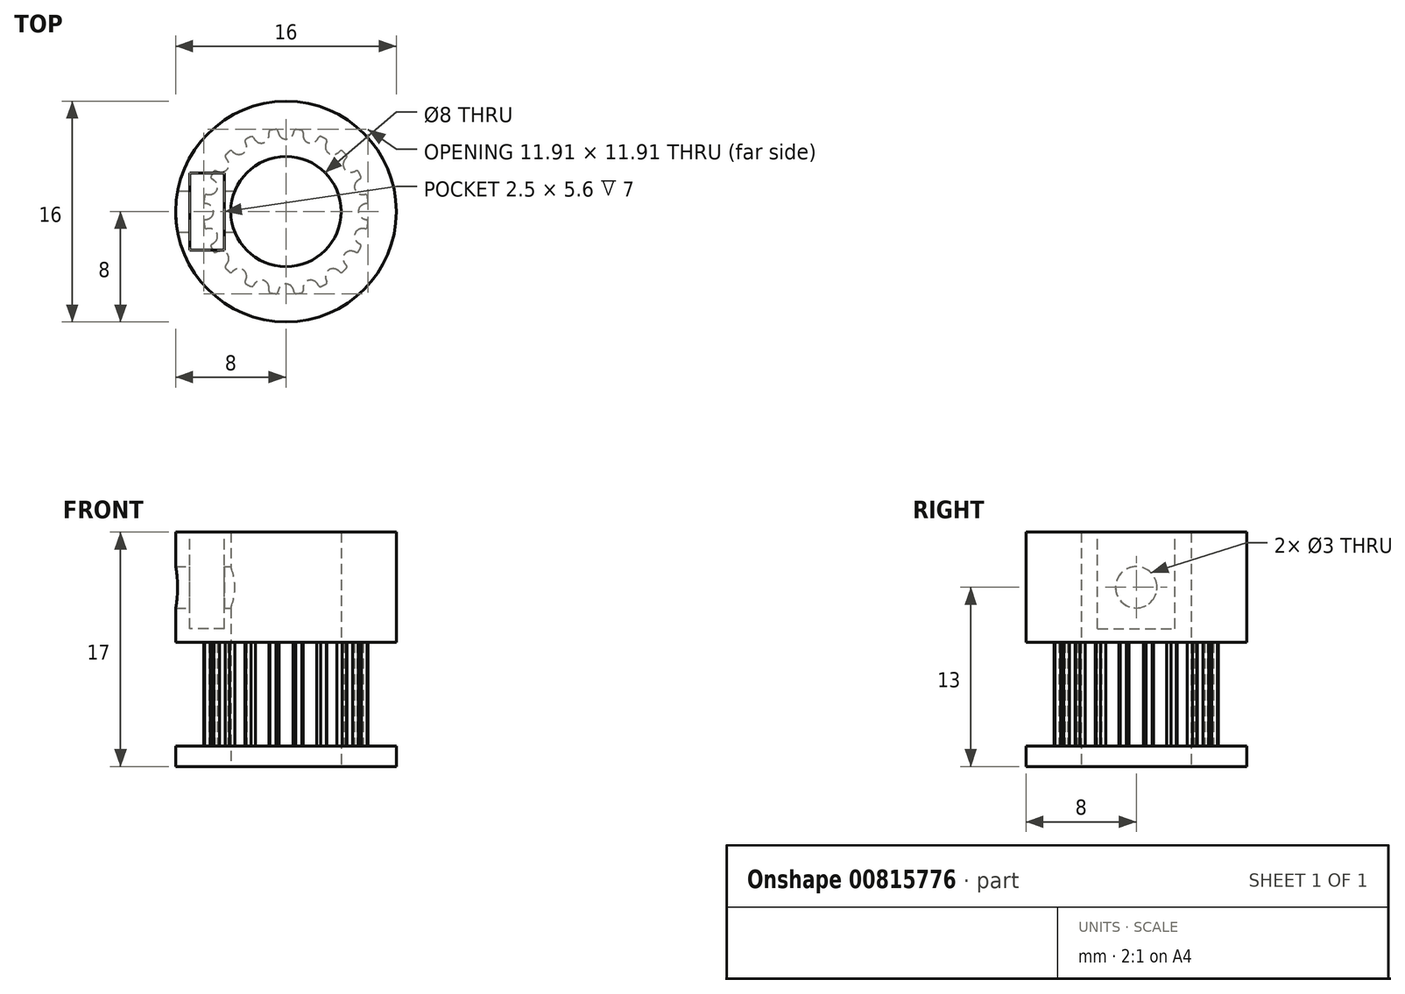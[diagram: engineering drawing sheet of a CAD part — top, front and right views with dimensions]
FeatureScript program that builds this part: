
annotation { "Feature Type Name" : "Feature", "Feature Type Description" : "" }
export const myFeature = defineFeature(function(context is Context, id is Id, definition is map)
    precondition{}
    {
        {
            var Q0;
            Q0=qCreatedBy(makeId("Top.planeOp"),FACE);
            var sketch = newSketch(context, id + "F0", { "sketchPlane" : qUnion([Q0])});
            skLineSegment(sketch, "E0", {"start": v(-19.17, 17.78) * mm, "end": v(-18.17, 17.78) * mm});
            skLineSegment(sketch, "E1", {"start": v(-18.17, 17.78) * mm, "end": v(-18.17, 18.4) * mm});
            skArc(sketch, "E2", {"start": v(-18.67, 18.85) * mm, "mid": v(-18.88, 19.07) * mm, "end": v(-19.17, 19.16) * mm});
            skArc(sketch, "E3", {"start": v(-18.58, 18.54) * mm, "mid": v(-18.61, 18.7) * mm, "end": v(-18.67, 18.85) * mm});
            skArc(sketch, "E4", {"start": v(-18.58, 18.54) * mm, "mid": v(-18.53, 18.44) * mm, "end": v(-18.43, 18.4) * mm});
            skLineSegment(sketch, "E5", {"start": v(-18.43, 18.4) * mm, "end": v(-18.17, 18.4) * mm});
            skArc(sketch, "E6.0.MirrorCS", {"start": v(-19.67, 18.85) * mm, "mid": v(-19.47, 19.07) * mm, "end": v(-19.17, 19.16) * mm});
            skArc(sketch, "E7.0.MirrorCS", {"start": v(-19.76, 18.54) * mm, "mid": v(-19.73, 18.7) * mm, "end": v(-19.67, 18.85) * mm});
            skArc(sketch, "E8.0.MirrorCS", {"start": v(-19.76, 18.54) * mm, "mid": v(-19.81, 18.44) * mm, "end": v(-19.91, 18.4) * mm});
            skLineSegment(sketch, "E9.0.MirrorCS", {"start": v(-19.91, 18.4) * mm, "end": v(-20.17, 18.4) * mm});
            skLineSegment(sketch, "E10.0.MirrorCS", {"start": v(-20.17, 17.78) * mm, "end": v(-20.17, 18.4) * mm});
            skLineSegment(sketch, "E11.0.MirrorCS", {"start": v(-19.17, 17.78) * mm, "end": v(-20.17, 17.78) * mm});
            skLineSegment(sketch, "E12.direction1", {"start": v(-20.17, 17.78) * mm, "end": v(-18.17, 17.78) * mm, "construction": true});
            skLineSegment(sketch, "E13", {"start": v(-20.17, 18.15) * mm, "end": v(-18.17, 18.15) * mm, "construction": true});
            skPoint(sketch, "E14", {"position": v(0, -5.25) * mm});
            skArc(sketch, "E15", {"start": v(0.51, -5.6) * mm, "mid": v(0, -5.25) * mm, "end": v(-0.51, -5.6) * mm});
            skArc(sketch, "E16", {"start": v(-0.51, -5.6) * mm, "mid": v(-0.56, -5.71) * mm, "end": v(-0.59, -5.83) * mm});
            skArc(sketch, "E17", {"start": v(0.59, -5.83) * mm, "mid": v(0.56, -5.71) * mm, "end": v(0.51, -5.6) * mm});
            skArc(sketch, "E18", {"start": v(0.72, -5.96) * mm, "mid": v(0.94, -5.93) * mm, "end": v(1.16, -5.89) * mm});
            skArc(sketch, "E19", {"start": v(0.59, -5.83) * mm, "mid": v(0.66, -5.94) * mm, "end": v(0.8, -5.95) * mm});
            skArc(sketch, "E20", {"start": v(-0.59, -5.83) * mm, "mid": v(-0.66, -5.94) * mm, "end": v(-0.8, -5.95) * mm});
            skArc(sketch, "E21.1.0", {"start": v(2.22, -5.16) * mm, "mid": v(1.62, -5) * mm, "end": v(1.24, -5.48) * mm});
            skPoint(sketch, "E21.1.1", {"position": v(1.62, -5) * mm});
            skArc(sketch, "E21.1.2", {"start": v(1.24, -5.48) * mm, "mid": v(1.23, -5.6) * mm, "end": v(1.24, -5.73) * mm});
            skArc(sketch, "E21.1.3", {"start": v(2.36, -5.37) * mm, "mid": v(2.47, -5.44) * mm, "end": v(2.6, -5.41) * mm});
            skArc(sketch, "E21.1.4", {"start": v(1.24, -5.73) * mm, "mid": v(1.2, -5.85) * mm, "end": v(1.08, -5.9) * mm});
            skArc(sketch, "E21.1.5", {"start": v(2.36, -5.37) * mm, "mid": v(2.3, -5.26) * mm, "end": v(2.22, -5.16) * mm});
            skArc(sketch, "E22.3.2.0", {"start": v(3.7, -4.22) * mm, "mid": v(3.09, -4.25) * mm, "end": v(2.87, -4.83) * mm});
            skPoint(sketch, "E22.4.2.0", {"position": v(3.09, -4.25) * mm});
            skArc(sketch, "E22.5.2.0", {"start": v(2.87, -4.83) * mm, "mid": v(2.9, -4.95) * mm, "end": v(2.95, -5.07) * mm});
            skArc(sketch, "E22.9.2.0", {"start": v(3.9, -4.37) * mm, "mid": v(4.03, -4.41) * mm, "end": v(4.14, -4.35) * mm});
            skArc(sketch, "E22.13.2.0", {"start": v(2.95, -5.07) * mm, "mid": v(2.95, -5.2) * mm, "end": v(2.85, -5.28) * mm});
            skArc(sketch, "E22.17.2.0", {"start": v(3.9, -4.37) * mm, "mid": v(3.81, -4.3) * mm, "end": v(3.7, -4.22) * mm});
            skArc(sketch, "E22.3.3.0", {"start": v(4.83, -2.87) * mm, "mid": v(4.25, -3.09) * mm, "end": v(4.22, -3.7) * mm});
            skPoint(sketch, "E22.4.3.0", {"position": v(4.25, -3.09) * mm});
            skArc(sketch, "E22.5.3.0", {"start": v(4.22, -3.7) * mm, "mid": v(4.3, -3.81) * mm, "end": v(4.37, -3.9) * mm});
            skArc(sketch, "E22.9.3.0", {"start": v(5.07, -2.95) * mm, "mid": v(5.2, -2.95) * mm, "end": v(5.28, -2.85) * mm});
            skArc(sketch, "E22.13.3.0", {"start": v(4.37, -3.9) * mm, "mid": v(4.41, -4.03) * mm, "end": v(4.35, -4.14) * mm});
            skArc(sketch, "E22.17.3.0", {"start": v(5.07, -2.95) * mm, "mid": v(4.95, -2.9) * mm, "end": v(4.83, -2.87) * mm});
            skArc(sketch, "E22.3.4.0", {"start": v(5.48, -1.24) * mm, "mid": v(5, -1.62) * mm, "end": v(5.16, -2.22) * mm});
            skPoint(sketch, "E22.4.4.0", {"position": v(5, -1.62) * mm});
            skArc(sketch, "E22.5.4.0", {"start": v(5.16, -2.22) * mm, "mid": v(5.26, -2.3) * mm, "end": v(5.37, -2.36) * mm});
            skArc(sketch, "E22.9.4.0", {"start": v(5.73, -1.24) * mm, "mid": v(5.85, -1.2) * mm, "end": v(5.9, -1.08) * mm});
            skArc(sketch, "E22.13.4.0", {"start": v(5.37, -2.36) * mm, "mid": v(5.44, -2.47) * mm, "end": v(5.41, -2.6) * mm});
            skArc(sketch, "E22.17.4.0", {"start": v(5.73, -1.24) * mm, "mid": v(5.6, -1.23) * mm, "end": v(5.48, -1.24) * mm});
            skArc(sketch, "E22.3.5.0", {"start": v(5.6, 0.51) * mm, "mid": v(5.25, 0) * mm, "end": v(5.6, -0.51) * mm});
            skPoint(sketch, "E22.4.5.0", {"position": v(5.25, 0) * mm});
            skArc(sketch, "E22.5.5.0", {"start": v(5.6, -0.51) * mm, "mid": v(5.71, -0.56) * mm, "end": v(5.83, -0.59) * mm});
            skArc(sketch, "E22.9.5.0", {"start": v(5.83, 0.59) * mm, "mid": v(5.94, 0.66) * mm, "end": v(5.95, 0.8) * mm});
            skArc(sketch, "E22.13.5.0", {"start": v(5.83, -0.59) * mm, "mid": v(5.94, -0.66) * mm, "end": v(5.95, -0.8) * mm});
            skArc(sketch, "E22.17.5.0", {"start": v(5.83, 0.59) * mm, "mid": v(5.71, 0.56) * mm, "end": v(5.6, 0.51) * mm});
            skArc(sketch, "E22.3.6.0", {"start": v(5.16, 2.22) * mm, "mid": v(5, 1.62) * mm, "end": v(5.48, 1.24) * mm});
            skPoint(sketch, "E22.4.6.0", {"position": v(5, 1.62) * mm});
            skArc(sketch, "E22.5.6.0", {"start": v(5.48, 1.24) * mm, "mid": v(5.6, 1.23) * mm, "end": v(5.73, 1.24) * mm});
            skArc(sketch, "E22.9.6.0", {"start": v(5.37, 2.36) * mm, "mid": v(5.44, 2.47) * mm, "end": v(5.41, 2.6) * mm});
            skArc(sketch, "E22.13.6.0", {"start": v(5.73, 1.24) * mm, "mid": v(5.85, 1.2) * mm, "end": v(5.9, 1.08) * mm});
            skArc(sketch, "E22.17.6.0", {"start": v(5.37, 2.36) * mm, "mid": v(5.26, 2.3) * mm, "end": v(5.16, 2.22) * mm});
            skArc(sketch, "E22.3.7.0", {"start": v(4.22, 3.7) * mm, "mid": v(4.25, 3.09) * mm, "end": v(4.83, 2.87) * mm});
            skPoint(sketch, "E22.4.7.0", {"position": v(4.25, 3.09) * mm});
            skArc(sketch, "E22.5.7.0", {"start": v(4.83, 2.87) * mm, "mid": v(4.95, 2.9) * mm, "end": v(5.07, 2.95) * mm});
            skArc(sketch, "E22.9.7.0", {"start": v(4.37, 3.9) * mm, "mid": v(4.41, 4.03) * mm, "end": v(4.35, 4.14) * mm});
            skArc(sketch, "E22.13.7.0", {"start": v(5.07, 2.95) * mm, "mid": v(5.2, 2.95) * mm, "end": v(5.28, 2.85) * mm});
            skArc(sketch, "E22.17.7.0", {"start": v(4.37, 3.9) * mm, "mid": v(4.3, 3.81) * mm, "end": v(4.22, 3.7) * mm});
            skArc(sketch, "E22.3.8.0", {"start": v(2.87, 4.83) * mm, "mid": v(3.09, 4.25) * mm, "end": v(3.7, 4.22) * mm});
            skPoint(sketch, "E22.4.8.0", {"position": v(3.09, 4.25) * mm});
            skArc(sketch, "E22.5.8.0", {"start": v(3.7, 4.22) * mm, "mid": v(3.81, 4.3) * mm, "end": v(3.9, 4.37) * mm});
            skArc(sketch, "E22.9.8.0", {"start": v(2.95, 5.07) * mm, "mid": v(2.95, 5.2) * mm, "end": v(2.85, 5.28) * mm});
            skArc(sketch, "E22.13.8.0", {"start": v(3.9, 4.37) * mm, "mid": v(4.03, 4.41) * mm, "end": v(4.14, 4.35) * mm});
            skArc(sketch, "E22.17.8.0", {"start": v(2.95, 5.07) * mm, "mid": v(2.9, 4.95) * mm, "end": v(2.87, 4.83) * mm});
            skArc(sketch, "E22.3.9.0", {"start": v(1.24, 5.48) * mm, "mid": v(1.62, 5) * mm, "end": v(2.22, 5.16) * mm});
            skPoint(sketch, "E22.4.9.0", {"position": v(1.62, 5) * mm});
            skArc(sketch, "E22.5.9.0", {"start": v(2.22, 5.16) * mm, "mid": v(2.3, 5.26) * mm, "end": v(2.36, 5.37) * mm});
            skArc(sketch, "E22.9.9.0", {"start": v(1.24, 5.73) * mm, "mid": v(1.2, 5.85) * mm, "end": v(1.08, 5.9) * mm});
            skArc(sketch, "E22.13.9.0", {"start": v(2.36, 5.37) * mm, "mid": v(2.47, 5.44) * mm, "end": v(2.6, 5.41) * mm});
            skArc(sketch, "E22.17.9.0", {"start": v(1.24, 5.73) * mm, "mid": v(1.23, 5.6) * mm, "end": v(1.24, 5.48) * mm});
            skArc(sketch, "E22.3.10.0", {"start": v(-0.51, 5.6) * mm, "mid": v(0, 5.25) * mm, "end": v(0.51, 5.6) * mm});
            skPoint(sketch, "E22.4.10.0", {"position": v(0, 5.25) * mm});
            skArc(sketch, "E22.5.10.0", {"start": v(0.51, 5.6) * mm, "mid": v(0.56, 5.71) * mm, "end": v(0.59, 5.83) * mm});
            skArc(sketch, "E22.9.10.0", {"start": v(-0.59, 5.83) * mm, "mid": v(-0.66, 5.94) * mm, "end": v(-0.8, 5.95) * mm});
            skArc(sketch, "E22.13.10.0", {"start": v(0.59, 5.83) * mm, "mid": v(0.66, 5.94) * mm, "end": v(0.8, 5.95) * mm});
            skArc(sketch, "E22.17.10.0", {"start": v(-0.59, 5.83) * mm, "mid": v(-0.56, 5.71) * mm, "end": v(-0.51, 5.6) * mm});
            skArc(sketch, "E22.3.11.0", {"start": v(-2.22, 5.16) * mm, "mid": v(-1.62, 5) * mm, "end": v(-1.24, 5.48) * mm});
            skPoint(sketch, "E22.4.11.0", {"position": v(-1.62, 5) * mm});
            skArc(sketch, "E22.5.11.0", {"start": v(-1.24, 5.48) * mm, "mid": v(-1.23, 5.6) * mm, "end": v(-1.24, 5.73) * mm});
            skArc(sketch, "E22.9.11.0", {"start": v(-2.36, 5.37) * mm, "mid": v(-2.47, 5.44) * mm, "end": v(-2.6, 5.41) * mm});
            skArc(sketch, "E22.13.11.0", {"start": v(-1.24, 5.73) * mm, "mid": v(-1.2, 5.85) * mm, "end": v(-1.08, 5.9) * mm});
            skArc(sketch, "E22.17.11.0", {"start": v(-2.36, 5.37) * mm, "mid": v(-2.3, 5.26) * mm, "end": v(-2.22, 5.16) * mm});
            skArc(sketch, "E22.3.12.0", {"start": v(-3.7, 4.22) * mm, "mid": v(-3.09, 4.25) * mm, "end": v(-2.87, 4.83) * mm});
            skPoint(sketch, "E22.4.12.0", {"position": v(-3.09, 4.25) * mm});
            skArc(sketch, "E22.5.12.0", {"start": v(-2.87, 4.83) * mm, "mid": v(-2.9, 4.95) * mm, "end": v(-2.95, 5.07) * mm});
            skArc(sketch, "E22.9.12.0", {"start": v(-3.9, 4.37) * mm, "mid": v(-4.03, 4.41) * mm, "end": v(-4.14, 4.35) * mm});
            skArc(sketch, "E22.13.12.0", {"start": v(-2.95, 5.07) * mm, "mid": v(-2.95, 5.2) * mm, "end": v(-2.85, 5.28) * mm});
            skArc(sketch, "E22.17.12.0", {"start": v(-3.9, 4.37) * mm, "mid": v(-3.81, 4.3) * mm, "end": v(-3.7, 4.22) * mm});
            skArc(sketch, "E22.3.13.0", {"start": v(-4.83, 2.87) * mm, "mid": v(-4.25, 3.09) * mm, "end": v(-4.22, 3.7) * mm});
            skPoint(sketch, "E22.4.13.0", {"position": v(-4.25, 3.09) * mm});
            skArc(sketch, "E22.5.13.0", {"start": v(-4.22, 3.7) * mm, "mid": v(-4.3, 3.81) * mm, "end": v(-4.37, 3.9) * mm});
            skArc(sketch, "E22.9.13.0", {"start": v(-5.07, 2.95) * mm, "mid": v(-5.2, 2.95) * mm, "end": v(-5.28, 2.85) * mm});
            skArc(sketch, "E22.13.13.0", {"start": v(-4.37, 3.9) * mm, "mid": v(-4.41, 4.03) * mm, "end": v(-4.35, 4.14) * mm});
            skArc(sketch, "E22.17.13.0", {"start": v(-5.07, 2.95) * mm, "mid": v(-4.95, 2.9) * mm, "end": v(-4.83, 2.87) * mm});
            skArc(sketch, "E22.3.14.0", {"start": v(-5.48, 1.24) * mm, "mid": v(-5, 1.62) * mm, "end": v(-5.16, 2.22) * mm});
            skPoint(sketch, "E22.4.14.0", {"position": v(-5, 1.62) * mm});
            skArc(sketch, "E22.5.14.0", {"start": v(-5.16, 2.22) * mm, "mid": v(-5.26, 2.3) * mm, "end": v(-5.37, 2.36) * mm});
            skArc(sketch, "E22.9.14.0", {"start": v(-5.73, 1.24) * mm, "mid": v(-5.85, 1.2) * mm, "end": v(-5.9, 1.08) * mm});
            skArc(sketch, "E22.13.14.0", {"start": v(-5.37, 2.36) * mm, "mid": v(-5.44, 2.47) * mm, "end": v(-5.41, 2.6) * mm});
            skArc(sketch, "E22.17.14.0", {"start": v(-5.73, 1.24) * mm, "mid": v(-5.6, 1.23) * mm, "end": v(-5.48, 1.24) * mm});
            skArc(sketch, "E22.3.15.0", {"start": v(-5.6, -0.51) * mm, "mid": v(-5.25, 0) * mm, "end": v(-5.6, 0.51) * mm});
            skPoint(sketch, "E22.4.15.0", {"position": v(-5.25, 0) * mm});
            skArc(sketch, "E22.5.15.0", {"start": v(-5.6, 0.51) * mm, "mid": v(-5.71, 0.56) * mm, "end": v(-5.83, 0.59) * mm});
            skArc(sketch, "E22.9.15.0", {"start": v(-5.83, -0.59) * mm, "mid": v(-5.94, -0.66) * mm, "end": v(-5.95, -0.8) * mm});
            skArc(sketch, "E22.13.15.0", {"start": v(-5.83, 0.59) * mm, "mid": v(-5.94, 0.66) * mm, "end": v(-5.95, 0.8) * mm});
            skArc(sketch, "E22.17.15.0", {"start": v(-5.83, -0.59) * mm, "mid": v(-5.71, -0.56) * mm, "end": v(-5.6, -0.51) * mm});
            skArc(sketch, "E22.3.16.0", {"start": v(-5.16, -2.22) * mm, "mid": v(-5, -1.62) * mm, "end": v(-5.48, -1.24) * mm});
            skPoint(sketch, "E22.4.16.0", {"position": v(-5, -1.62) * mm});
            skArc(sketch, "E22.5.16.0", {"start": v(-5.48, -1.24) * mm, "mid": v(-5.6, -1.23) * mm, "end": v(-5.73, -1.24) * mm});
            skArc(sketch, "E22.9.16.0", {"start": v(-5.37, -2.36) * mm, "mid": v(-5.44, -2.47) * mm, "end": v(-5.41, -2.6) * mm});
            skArc(sketch, "E22.13.16.0", {"start": v(-5.73, -1.24) * mm, "mid": v(-5.85, -1.2) * mm, "end": v(-5.9, -1.08) * mm});
            skArc(sketch, "E22.17.16.0", {"start": v(-5.37, -2.36) * mm, "mid": v(-5.26, -2.3) * mm, "end": v(-5.16, -2.22) * mm});
            skArc(sketch, "E22.3.17.0", {"start": v(-4.22, -3.7) * mm, "mid": v(-4.25, -3.09) * mm, "end": v(-4.83, -2.87) * mm});
            skPoint(sketch, "E22.4.17.0", {"position": v(-4.25, -3.09) * mm});
            skArc(sketch, "E22.5.17.0", {"start": v(-4.83, -2.87) * mm, "mid": v(-4.95, -2.9) * mm, "end": v(-5.07, -2.95) * mm});
            skArc(sketch, "E22.9.17.0", {"start": v(-4.37, -3.9) * mm, "mid": v(-4.41, -4.03) * mm, "end": v(-4.35, -4.14) * mm});
            skArc(sketch, "E22.13.17.0", {"start": v(-5.07, -2.95) * mm, "mid": v(-5.2, -2.95) * mm, "end": v(-5.28, -2.85) * mm});
            skArc(sketch, "E22.17.17.0", {"start": v(-4.37, -3.9) * mm, "mid": v(-4.3, -3.81) * mm, "end": v(-4.22, -3.7) * mm});
            skArc(sketch, "E22.3.18.0", {"start": v(-2.87, -4.83) * mm, "mid": v(-3.09, -4.25) * mm, "end": v(-3.7, -4.22) * mm});
            skPoint(sketch, "E22.4.18.0", {"position": v(-3.09, -4.25) * mm});
            skArc(sketch, "E22.5.18.0", {"start": v(-3.7, -4.22) * mm, "mid": v(-3.81, -4.3) * mm, "end": v(-3.9, -4.37) * mm});
            skArc(sketch, "E22.9.18.0", {"start": v(-2.95, -5.07) * mm, "mid": v(-2.95, -5.2) * mm, "end": v(-2.85, -5.28) * mm});
            skArc(sketch, "E22.13.18.0", {"start": v(-3.9, -4.37) * mm, "mid": v(-4.03, -4.41) * mm, "end": v(-4.14, -4.35) * mm});
            skArc(sketch, "E22.17.18.0", {"start": v(-2.95, -5.07) * mm, "mid": v(-2.9, -4.95) * mm, "end": v(-2.87, -4.83) * mm});
            skArc(sketch, "E22.3.19.0", {"start": v(-1.24, -5.48) * mm, "mid": v(-1.62, -5) * mm, "end": v(-2.22, -5.16) * mm});
            skPoint(sketch, "E22.4.19.0", {"position": v(-1.62, -5) * mm});
            skArc(sketch, "E22.5.19.0", {"start": v(-2.22, -5.16) * mm, "mid": v(-2.3, -5.26) * mm, "end": v(-2.36, -5.37) * mm});
            skArc(sketch, "E22.9.19.0", {"start": v(-1.24, -5.73) * mm, "mid": v(-1.2, -5.85) * mm, "end": v(-1.08, -5.9) * mm});
            skArc(sketch, "E22.13.19.0", {"start": v(-2.36, -5.37) * mm, "mid": v(-2.47, -5.44) * mm, "end": v(-2.6, -5.41) * mm});
            skArc(sketch, "E22.17.19.0", {"start": v(-1.24, -5.73) * mm, "mid": v(-1.23, -5.6) * mm, "end": v(-1.24, -5.48) * mm});
            skArc(sketch, "E23.trimOffspring", {"start": v(2.52, -5.44) * mm, "mid": v(2.72, -5.35) * mm, "end": v(2.92, -5.24) * mm});
            skArc(sketch, "E24.trimOffspring", {"start": v(4.08, -4.4) * mm, "mid": v(4.24, -4.24) * mm, "end": v(4.4, -4.08) * mm});
            skArc(sketch, "E25.trimOffspring", {"start": v(5.24, -2.92) * mm, "mid": v(5.33, -2.76) * mm, "end": v(5.41, -2.6) * mm});
            skArc(sketch, "E26.trimOffspring", {"start": v(5.89, -1.16) * mm, "mid": v(5.93, -0.94) * mm, "end": v(5.96, -0.72) * mm});
            skArc(sketch, "E27.trimOffspring", {"start": v(5.44, 2.52) * mm, "mid": v(5.35, 2.72) * mm, "end": v(5.24, 2.92) * mm});
            skArc(sketch, "E28.trimOffspring", {"start": v(4.4, 4.08) * mm, "mid": v(4.24, 4.24) * mm, "end": v(4.08, 4.4) * mm});
            skArc(sketch, "E29.trimOffspring", {"start": v(5.96, 0.72) * mm, "mid": v(5.93, 0.94) * mm, "end": v(5.89, 1.16) * mm});
            skArc(sketch, "E30.trimOffspring", {"start": v(2.92, 5.24) * mm, "mid": v(2.72, 5.35) * mm, "end": v(2.52, 5.44) * mm});
            skArc(sketch, "E31.trimOffspring", {"start": v(1.16, 5.89) * mm, "mid": v(0.94, 5.93) * mm, "end": v(0.72, 5.96) * mm});
            skArc(sketch, "E32.trimOffspring", {"start": v(-0.72, 5.96) * mm, "mid": v(-0.94, 5.93) * mm, "end": v(-1.16, 5.89) * mm});
            skArc(sketch, "E33.trimOffspring", {"start": v(-2.52, 5.44) * mm, "mid": v(-2.72, 5.35) * mm, "end": v(-2.92, 5.24) * mm});
            skArc(sketch, "E34.trimOffspring", {"start": v(-4.08, 4.4) * mm, "mid": v(-4.24, 4.24) * mm, "end": v(-4.4, 4.08) * mm});
            skArc(sketch, "E35.trimOffspring", {"start": v(-5.24, 2.92) * mm, "mid": v(-5.35, 2.72) * mm, "end": v(-5.44, 2.52) * mm});
            skArc(sketch, "E36.trimOffspring", {"start": v(-5.89, 1.16) * mm, "mid": v(-5.93, 0.94) * mm, "end": v(-5.96, 0.72) * mm});
            skArc(sketch, "E37.trimOffspring", {"start": v(-5.96, -0.72) * mm, "mid": v(-5.93, -0.94) * mm, "end": v(-5.89, -1.16) * mm});
            skArc(sketch, "E38.trimOffspring", {"start": v(-5.44, -2.52) * mm, "mid": v(-5.35, -2.72) * mm, "end": v(-5.24, -2.92) * mm});
            skArc(sketch, "E39.trimOffspring", {"start": v(-4.4, -4.08) * mm, "mid": v(-4.24, -4.24) * mm, "end": v(-4.08, -4.4) * mm});
            skArc(sketch, "E40.trimOffspring", {"start": v(-2.92, -5.24) * mm, "mid": v(-2.72, -5.35) * mm, "end": v(-2.52, -5.44) * mm});
            skArc(sketch, "E41.trimOffspring", {"start": v(-1.16, -5.89) * mm, "mid": v(-0.94, -5.93) * mm, "end": v(-0.72, -5.96) * mm});
            skSolve(sketch);
        }
        {
            var Q0;
            Q0=makeQuery(id+"F0.imprint","IMPRINT",FACE,{"disambiguationData":[TD([[makeQuery(id+"F0.imprint","IMPRINT",EDGE,{"derivedFrom":sQuery(id+"F0.wireOp",EDGE,"E15")}),-1.0]])]});
            extrude(context, id + "F1", {"entities" : qUnion([Q0]), "depth" : 7.5 * mm});
        }
        {
            var Q0;
            Q0=makeQuery(id+"F1.opExtrude","CAP_FACE",FACE,{"disambiguationData":[OSD([sQuery(id+"F0.wireOp",EDGE,"E15"),sQuery(id+"F0.wireOp",EDGE,"E16"),sQuery(id+"F0.wireOp",EDGE,"E17"),sQuery(id+"F0.wireOp",EDGE,"E18"),sQuery(id+"F0.wireOp",EDGE,"E19"),sQuery(id+"F0.wireOp",EDGE,"E20"),sQuery(id+"F0.wireOp",EDGE,"E21.1.0"),sQuery(id+"F0.wireOp",EDGE,"E21.1.2"),sQuery(id+"F0.wireOp",EDGE,"E21.1.3"),sQuery(id+"F0.wireOp",EDGE,"E21.1.4"),sQuery(id+"F0.wireOp",EDGE,"E21.1.5"),sQuery(id+"F0.wireOp",EDGE,"E22.3.2.0"),sQuery(id+"F0.wireOp",EDGE,"E22.5.2.0"),sQuery(id+"F0.wireOp",EDGE,"E22.9.2.0"),sQuery(id+"F0.wireOp",EDGE,"E22.13.2.0"),sQuery(id+"F0.wireOp",EDGE,"E22.17.2.0"),sQuery(id+"F0.wireOp",EDGE,"E22.3.3.0"),sQuery(id+"F0.wireOp",EDGE,"E22.5.3.0"),sQuery(id+"F0.wireOp",EDGE,"E22.9.3.0"),sQuery(id+"F0.wireOp",EDGE,"E22.13.3.0"),sQuery(id+"F0.wireOp",EDGE,"E22.17.3.0"),sQuery(id+"F0.wireOp",EDGE,"E22.3.4.0"),sQuery(id+"F0.wireOp",EDGE,"E22.5.4.0"),sQuery(id+"F0.wireOp",EDGE,"E22.9.4.0"),sQuery(id+"F0.wireOp",EDGE,"E22.13.4.0"),sQuery(id+"F0.wireOp",EDGE,"E22.17.4.0"),sQuery(id+"F0.wireOp",EDGE,"E22.3.5.0"),sQuery(id+"F0.wireOp",EDGE,"E22.5.5.0"),sQuery(id+"F0.wireOp",EDGE,"E22.9.5.0"),sQuery(id+"F0.wireOp",EDGE,"E22.13.5.0"),sQuery(id+"F0.wireOp",EDGE,"E22.17.5.0"),sQuery(id+"F0.wireOp",EDGE,"E22.3.6.0"),sQuery(id+"F0.wireOp",EDGE,"E22.5.6.0"),sQuery(id+"F0.wireOp",EDGE,"E22.9.6.0"),sQuery(id+"F0.wireOp",EDGE,"E22.13.6.0"),sQuery(id+"F0.wireOp",EDGE,"E22.17.6.0"),sQuery(id+"F0.wireOp",EDGE,"E22.3.7.0"),sQuery(id+"F0.wireOp",EDGE,"E22.5.7.0"),sQuery(id+"F0.wireOp",EDGE,"E22.9.7.0"),sQuery(id+"F0.wireOp",EDGE,"E22.13.7.0"),sQuery(id+"F0.wireOp",EDGE,"E22.17.7.0"),sQuery(id+"F0.wireOp",EDGE,"E22.3.8.0"),sQuery(id+"F0.wireOp",EDGE,"E22.5.8.0"),sQuery(id+"F0.wireOp",EDGE,"E22.9.8.0"),sQuery(id+"F0.wireOp",EDGE,"E22.13.8.0"),sQuery(id+"F0.wireOp",EDGE,"E22.17.8.0"),sQuery(id+"F0.wireOp",EDGE,"E22.3.9.0"),sQuery(id+"F0.wireOp",EDGE,"E22.5.9.0"),sQuery(id+"F0.wireOp",EDGE,"E22.9.9.0"),sQuery(id+"F0.wireOp",EDGE,"E22.13.9.0"),sQuery(id+"F0.wireOp",EDGE,"E22.17.9.0"),sQuery(id+"F0.wireOp",EDGE,"E22.3.10.0"),sQuery(id+"F0.wireOp",EDGE,"E22.5.10.0"),sQuery(id+"F0.wireOp",EDGE,"E22.9.10.0"),sQuery(id+"F0.wireOp",EDGE,"E22.13.10.0"),sQuery(id+"F0.wireOp",EDGE,"E22.17.10.0"),sQuery(id+"F0.wireOp",EDGE,"E22.3.11.0"),sQuery(id+"F0.wireOp",EDGE,"E22.5.11.0"),sQuery(id+"F0.wireOp",EDGE,"E22.9.11.0"),sQuery(id+"F0.wireOp",EDGE,"E22.13.11.0"),sQuery(id+"F0.wireOp",EDGE,"E22.17.11.0"),sQuery(id+"F0.wireOp",EDGE,"E22.3.12.0"),sQuery(id+"F0.wireOp",EDGE,"E22.5.12.0"),sQuery(id+"F0.wireOp",EDGE,"E22.9.12.0"),sQuery(id+"F0.wireOp",EDGE,"E22.13.12.0"),sQuery(id+"F0.wireOp",EDGE,"E22.17.12.0"),sQuery(id+"F0.wireOp",EDGE,"E22.3.13.0"),sQuery(id+"F0.wireOp",EDGE,"E22.5.13.0"),sQuery(id+"F0.wireOp",EDGE,"E22.9.13.0"),sQuery(id+"F0.wireOp",EDGE,"E22.13.13.0"),sQuery(id+"F0.wireOp",EDGE,"E22.17.13.0"),sQuery(id+"F0.wireOp",EDGE,"E22.3.14.0"),sQuery(id+"F0.wireOp",EDGE,"E22.5.14.0"),sQuery(id+"F0.wireOp",EDGE,"E22.9.14.0"),sQuery(id+"F0.wireOp",EDGE,"E22.13.14.0"),sQuery(id+"F0.wireOp",EDGE,"E22.17.14.0"),sQuery(id+"F0.wireOp",EDGE,"E22.3.15.0"),sQuery(id+"F0.wireOp",EDGE,"E22.5.15.0"),sQuery(id+"F0.wireOp",EDGE,"E22.9.15.0"),sQuery(id+"F0.wireOp",EDGE,"E22.13.15.0"),sQuery(id+"F0.wireOp",EDGE,"E22.17.15.0"),sQuery(id+"F0.wireOp",EDGE,"E22.3.16.0"),sQuery(id+"F0.wireOp",EDGE,"E22.5.16.0"),sQuery(id+"F0.wireOp",EDGE,"E22.9.16.0"),sQuery(id+"F0.wireOp",EDGE,"E22.13.16.0"),sQuery(id+"F0.wireOp",EDGE,"E22.17.16.0"),sQuery(id+"F0.wireOp",EDGE,"E22.3.17.0"),sQuery(id+"F0.wireOp",EDGE,"E22.5.17.0"),sQuery(id+"F0.wireOp",EDGE,"E22.9.17.0"),sQuery(id+"F0.wireOp",EDGE,"E22.13.17.0"),sQuery(id+"F0.wireOp",EDGE,"E22.17.17.0"),sQuery(id+"F0.wireOp",EDGE,"E22.3.18.0"),sQuery(id+"F0.wireOp",EDGE,"E22.5.18.0"),sQuery(id+"F0.wireOp",EDGE,"E22.9.18.0"),sQuery(id+"F0.wireOp",EDGE,"E22.13.18.0"),sQuery(id+"F0.wireOp",EDGE,"E22.17.18.0"),sQuery(id+"F0.wireOp",EDGE,"E22.3.19.0"),sQuery(id+"F0.wireOp",EDGE,"E22.5.19.0"),sQuery(id+"F0.wireOp",EDGE,"E22.9.19.0"),sQuery(id+"F0.wireOp",EDGE,"E22.13.19.0"),sQuery(id+"F0.wireOp",EDGE,"E22.17.19.0"),sQuery(id+"F0.wireOp",EDGE,"E23.trimOffspring"),sQuery(id+"F0.wireOp",EDGE,"E24.trimOffspring"),sQuery(id+"F0.wireOp",EDGE,"E25.trimOffspring"),sQuery(id+"F0.wireOp",EDGE,"E26.trimOffspring"),sQuery(id+"F0.wireOp",EDGE,"E27.trimOffspring"),sQuery(id+"F0.wireOp",EDGE,"E28.trimOffspring"),sQuery(id+"F0.wireOp",EDGE,"E29.trimOffspring"),sQuery(id+"F0.wireOp",EDGE,"E30.trimOffspring"),sQuery(id+"F0.wireOp",EDGE,"E31.trimOffspring"),sQuery(id+"F0.wireOp",EDGE,"E32.trimOffspring"),sQuery(id+"F0.wireOp",EDGE,"E33.trimOffspring"),sQuery(id+"F0.wireOp",EDGE,"E34.trimOffspring"),sQuery(id+"F0.wireOp",EDGE,"E35.trimOffspring"),sQuery(id+"F0.wireOp",EDGE,"E36.trimOffspring"),sQuery(id+"F0.wireOp",EDGE,"E37.trimOffspring"),sQuery(id+"F0.wireOp",EDGE,"E38.trimOffspring"),sQuery(id+"F0.wireOp",EDGE,"E39.trimOffspring"),sQuery(id+"F0.wireOp",EDGE,"E40.trimOffspring"),sQuery(id+"F0.wireOp",EDGE,"E41.trimOffspring")])],"isStart":false});
            var sketch = newSketch(context, id + "F2", { "sketchPlane" : qUnion([Q0])});
            skCircle(sketch, "E42", {"center": v(0, 0) * mm, "radius": 8 * mm});
            skSolve(sketch);
        }
        {
            var Q0;
            Q0=qSketchRegion(id+"F2",true);
            extrude(context, id + "F3", {"entities" : qUnion([Q0]), "operationType" : NewBodyOperationType.ADD, "depth" : 8 * mm});
        }
        {
            var Q0;
            Q0=makeQuery(id+"F1.opExtrude","CAP_FACE",FACE,{"disambiguationData":[OSD([sQuery(id+"F0.wireOp",EDGE,"E15"),sQuery(id+"F0.wireOp",EDGE,"E16"),sQuery(id+"F0.wireOp",EDGE,"E17"),sQuery(id+"F0.wireOp",EDGE,"E18"),sQuery(id+"F0.wireOp",EDGE,"E19"),sQuery(id+"F0.wireOp",EDGE,"E20"),sQuery(id+"F0.wireOp",EDGE,"E21.1.0"),sQuery(id+"F0.wireOp",EDGE,"E21.1.2"),sQuery(id+"F0.wireOp",EDGE,"E21.1.3"),sQuery(id+"F0.wireOp",EDGE,"E21.1.4"),sQuery(id+"F0.wireOp",EDGE,"E21.1.5"),sQuery(id+"F0.wireOp",EDGE,"E22.3.2.0"),sQuery(id+"F0.wireOp",EDGE,"E22.5.2.0"),sQuery(id+"F0.wireOp",EDGE,"E22.9.2.0"),sQuery(id+"F0.wireOp",EDGE,"E22.13.2.0"),sQuery(id+"F0.wireOp",EDGE,"E22.17.2.0"),sQuery(id+"F0.wireOp",EDGE,"E22.3.3.0"),sQuery(id+"F0.wireOp",EDGE,"E22.5.3.0"),sQuery(id+"F0.wireOp",EDGE,"E22.9.3.0"),sQuery(id+"F0.wireOp",EDGE,"E22.13.3.0"),sQuery(id+"F0.wireOp",EDGE,"E22.17.3.0"),sQuery(id+"F0.wireOp",EDGE,"E22.3.4.0"),sQuery(id+"F0.wireOp",EDGE,"E22.5.4.0"),sQuery(id+"F0.wireOp",EDGE,"E22.9.4.0"),sQuery(id+"F0.wireOp",EDGE,"E22.13.4.0"),sQuery(id+"F0.wireOp",EDGE,"E22.17.4.0"),sQuery(id+"F0.wireOp",EDGE,"E22.3.5.0"),sQuery(id+"F0.wireOp",EDGE,"E22.5.5.0"),sQuery(id+"F0.wireOp",EDGE,"E22.9.5.0"),sQuery(id+"F0.wireOp",EDGE,"E22.13.5.0"),sQuery(id+"F0.wireOp",EDGE,"E22.17.5.0"),sQuery(id+"F0.wireOp",EDGE,"E22.3.6.0"),sQuery(id+"F0.wireOp",EDGE,"E22.5.6.0"),sQuery(id+"F0.wireOp",EDGE,"E22.9.6.0"),sQuery(id+"F0.wireOp",EDGE,"E22.13.6.0"),sQuery(id+"F0.wireOp",EDGE,"E22.17.6.0"),sQuery(id+"F0.wireOp",EDGE,"E22.3.7.0"),sQuery(id+"F0.wireOp",EDGE,"E22.5.7.0"),sQuery(id+"F0.wireOp",EDGE,"E22.9.7.0"),sQuery(id+"F0.wireOp",EDGE,"E22.13.7.0"),sQuery(id+"F0.wireOp",EDGE,"E22.17.7.0"),sQuery(id+"F0.wireOp",EDGE,"E22.3.8.0"),sQuery(id+"F0.wireOp",EDGE,"E22.5.8.0"),sQuery(id+"F0.wireOp",EDGE,"E22.9.8.0"),sQuery(id+"F0.wireOp",EDGE,"E22.13.8.0"),sQuery(id+"F0.wireOp",EDGE,"E22.17.8.0"),sQuery(id+"F0.wireOp",EDGE,"E22.3.9.0"),sQuery(id+"F0.wireOp",EDGE,"E22.5.9.0"),sQuery(id+"F0.wireOp",EDGE,"E22.9.9.0"),sQuery(id+"F0.wireOp",EDGE,"E22.13.9.0"),sQuery(id+"F0.wireOp",EDGE,"E22.17.9.0"),sQuery(id+"F0.wireOp",EDGE,"E22.3.10.0"),sQuery(id+"F0.wireOp",EDGE,"E22.5.10.0"),sQuery(id+"F0.wireOp",EDGE,"E22.9.10.0"),sQuery(id+"F0.wireOp",EDGE,"E22.13.10.0"),sQuery(id+"F0.wireOp",EDGE,"E22.17.10.0"),sQuery(id+"F0.wireOp",EDGE,"E22.3.11.0"),sQuery(id+"F0.wireOp",EDGE,"E22.5.11.0"),sQuery(id+"F0.wireOp",EDGE,"E22.9.11.0"),sQuery(id+"F0.wireOp",EDGE,"E22.13.11.0"),sQuery(id+"F0.wireOp",EDGE,"E22.17.11.0"),sQuery(id+"F0.wireOp",EDGE,"E22.3.12.0"),sQuery(id+"F0.wireOp",EDGE,"E22.5.12.0"),sQuery(id+"F0.wireOp",EDGE,"E22.9.12.0"),sQuery(id+"F0.wireOp",EDGE,"E22.13.12.0"),sQuery(id+"F0.wireOp",EDGE,"E22.17.12.0"),sQuery(id+"F0.wireOp",EDGE,"E22.3.13.0"),sQuery(id+"F0.wireOp",EDGE,"E22.5.13.0"),sQuery(id+"F0.wireOp",EDGE,"E22.9.13.0"),sQuery(id+"F0.wireOp",EDGE,"E22.13.13.0"),sQuery(id+"F0.wireOp",EDGE,"E22.17.13.0"),sQuery(id+"F0.wireOp",EDGE,"E22.3.14.0"),sQuery(id+"F0.wireOp",EDGE,"E22.5.14.0"),sQuery(id+"F0.wireOp",EDGE,"E22.9.14.0"),sQuery(id+"F0.wireOp",EDGE,"E22.13.14.0"),sQuery(id+"F0.wireOp",EDGE,"E22.17.14.0"),sQuery(id+"F0.wireOp",EDGE,"E22.3.15.0"),sQuery(id+"F0.wireOp",EDGE,"E22.5.15.0"),sQuery(id+"F0.wireOp",EDGE,"E22.9.15.0"),sQuery(id+"F0.wireOp",EDGE,"E22.13.15.0"),sQuery(id+"F0.wireOp",EDGE,"E22.17.15.0"),sQuery(id+"F0.wireOp",EDGE,"E22.3.16.0"),sQuery(id+"F0.wireOp",EDGE,"E22.5.16.0"),sQuery(id+"F0.wireOp",EDGE,"E22.9.16.0"),sQuery(id+"F0.wireOp",EDGE,"E22.13.16.0"),sQuery(id+"F0.wireOp",EDGE,"E22.17.16.0"),sQuery(id+"F0.wireOp",EDGE,"E22.3.17.0"),sQuery(id+"F0.wireOp",EDGE,"E22.5.17.0"),sQuery(id+"F0.wireOp",EDGE,"E22.9.17.0"),sQuery(id+"F0.wireOp",EDGE,"E22.13.17.0"),sQuery(id+"F0.wireOp",EDGE,"E22.17.17.0"),sQuery(id+"F0.wireOp",EDGE,"E22.3.18.0"),sQuery(id+"F0.wireOp",EDGE,"E22.5.18.0"),sQuery(id+"F0.wireOp",EDGE,"E22.9.18.0"),sQuery(id+"F0.wireOp",EDGE,"E22.13.18.0"),sQuery(id+"F0.wireOp",EDGE,"E22.17.18.0"),sQuery(id+"F0.wireOp",EDGE,"E22.3.19.0"),sQuery(id+"F0.wireOp",EDGE,"E22.5.19.0"),sQuery(id+"F0.wireOp",EDGE,"E22.9.19.0"),sQuery(id+"F0.wireOp",EDGE,"E22.13.19.0"),sQuery(id+"F0.wireOp",EDGE,"E22.17.19.0"),sQuery(id+"F0.wireOp",EDGE,"E23.trimOffspring"),sQuery(id+"F0.wireOp",EDGE,"E24.trimOffspring"),sQuery(id+"F0.wireOp",EDGE,"E25.trimOffspring"),sQuery(id+"F0.wireOp",EDGE,"E26.trimOffspring"),sQuery(id+"F0.wireOp",EDGE,"E27.trimOffspring"),sQuery(id+"F0.wireOp",EDGE,"E28.trimOffspring"),sQuery(id+"F0.wireOp",EDGE,"E29.trimOffspring"),sQuery(id+"F0.wireOp",EDGE,"E30.trimOffspring"),sQuery(id+"F0.wireOp",EDGE,"E31.trimOffspring"),sQuery(id+"F0.wireOp",EDGE,"E32.trimOffspring"),sQuery(id+"F0.wireOp",EDGE,"E33.trimOffspring"),sQuery(id+"F0.wireOp",EDGE,"E34.trimOffspring"),sQuery(id+"F0.wireOp",EDGE,"E35.trimOffspring"),sQuery(id+"F0.wireOp",EDGE,"E36.trimOffspring"),sQuery(id+"F0.wireOp",EDGE,"E37.trimOffspring"),sQuery(id+"F0.wireOp",EDGE,"E38.trimOffspring"),sQuery(id+"F0.wireOp",EDGE,"E39.trimOffspring"),sQuery(id+"F0.wireOp",EDGE,"E40.trimOffspring"),sQuery(id+"F0.wireOp",EDGE,"E41.trimOffspring")])],"isStart":true});
            var sketch = newSketch(context, id + "F4", { "sketchPlane" : qUnion([Q0])});
            skCircle(sketch, "E43", {"center": v(0, 0) * mm, "radius": 8 * mm});
            skSolve(sketch);
        }
        {
            var Q0;
            Q0=qSketchRegion(id+"F4",true);
            extrude(context, id + "F5", {"entities" : qUnion([Q0]), "operationType" : NewBodyOperationType.ADD, "depth" : 1.5 * mm});
        }
        {
            var Q0;
            Q0=makeQuery(id+"F5.opExtrude","CAP_FACE",FACE,{"disambiguationData":[OSD([sQuery(id+"F4.wireOp",EDGE,"E43")])],"isStart":false});
            var sketch = newSketch(context, id + "F6", { "sketchPlane" : qUnion([Q0])});
            skCircle(sketch, "E44", {"center": v(0, 0) * mm, "radius": 4 * mm});
            skSolve(sketch);
        }
        {
            var Q0;
            Q0=qSketchRegion(id+"F6",true);
            extrude(context, id + "F7", {"entities" : qUnion([Q0]), "operationType" : NewBodyOperationType.REMOVE, "endBound" : BoundingType.THROUGH_ALL, "oppositeDirection" : true, "depth" : 25 * mm});
        }
        {
            var Q0;
            Q0=qCreatedBy(makeId("Right.planeOp"),FACE);
            var sketch = newSketch(context, id + "F8", { "sketchPlane" : qUnion([Q0])});
            skCircle(sketch, "E45", {"center": v(0, 11.5) * mm, "radius": 1.5 * mm});
            skSolve(sketch);
        }
        {
            var Q0;
            Q0=qSketchRegion(id+"F8",true);
            extrude(context, id + "F9", {"entities" : qUnion([Q0]), "operationType" : NewBodyOperationType.REMOVE, "endBound" : BoundingType.THROUGH_ALL, "oppositeDirection" : true, "depth" : 25 * mm});
        }
        {
            var Q0;
            Q0=makeQuery(id+"F3.opExtrude","CAP_FACE",FACE,{"disambiguationData":[OSD([sQuery(id+"F2.wireOp",EDGE,"E42")])],"isStart":false});
            var sketch = newSketch(context, id + "F10", { "sketchPlane" : qUnion([Q0])});
            skLineSegment(sketch, "E46.bottom", {"start": v(-4.47, -2.8) * mm, "end": v(-6.97, -2.8) * mm});
            skLineSegment(sketch, "E46.top", {"start": v(-4.47, 2.8) * mm, "end": v(-6.97, 2.8) * mm});
            skLineSegment(sketch, "E46.left", {"start": v(-4.47, -2.8) * mm, "end": v(-4.47, 2.8) * mm});
            skLineSegment(sketch, "E46.right", {"start": v(-6.97, -2.8) * mm, "end": v(-6.97, 2.8) * mm});
            skSolve(sketch);
        }
        {
            var Q0;
            Q0=qSketchRegion(id+"F10",true);
            extrude(context, id + "F11", {"entities" : qUnion([Q0]), "operationType" : NewBodyOperationType.REMOVE, "oppositeDirection" : true, "depth" : 7 * mm});
        }
    });
